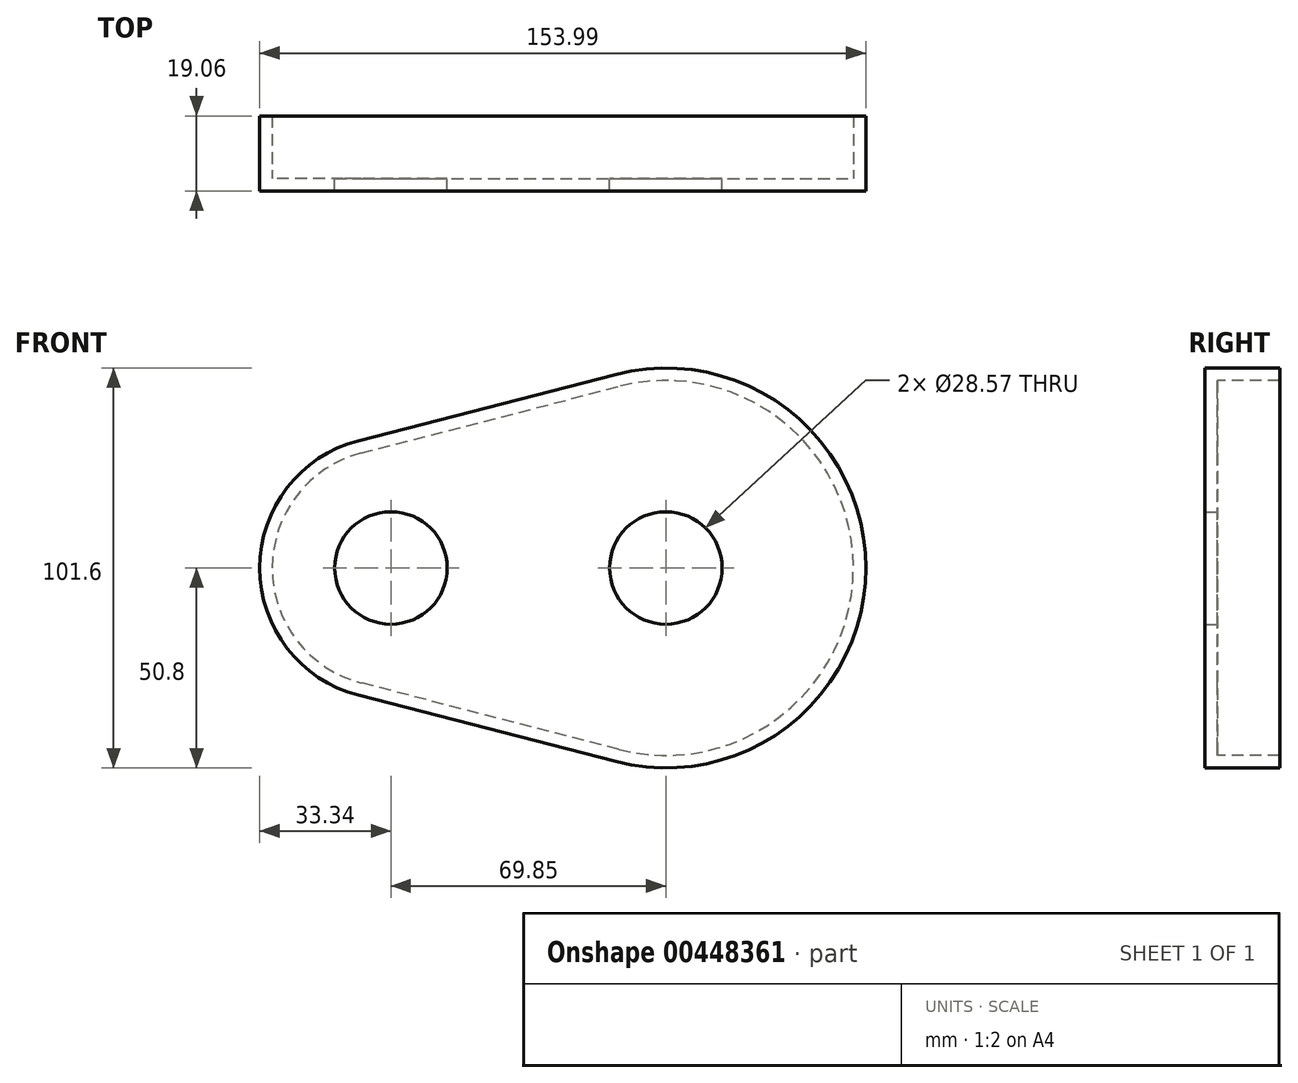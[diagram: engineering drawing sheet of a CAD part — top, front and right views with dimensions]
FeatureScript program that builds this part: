
annotation { "Feature Type Name" : "Feature", "Feature Type Description" : "" }
export const myFeature = defineFeature(function(context is Context, id is Id, definition is map)
    precondition{}
    {
        {
            var Q0;
            Q0=qCreatedBy(makeId("Front.planeOp"),FACE);
            var sketch = newSketch(context, id + "F0", { "sketchPlane" : qUnion([Q0])});
            skCircle(sketch, "E0", {"center": v(0, 0) * mm, "radius": 14.29 * mm});
            skLineSegment(sketch, "E1", {"start": v(0, 0) * mm, "end": v(-69.85, 0) * mm});
            skArc(sketch, "E2", {"start": v(-12.7, -49.19) * mm, "mid": v(50.8, 0) * mm, "end": v(-12.7, 49.19) * mm});
            skCircle(sketch, "E3", {"center": v(-69.85, 0) * mm, "radius": 14.29 * mm});
            skArc(sketch, "E4", {"start": v(-78.18, 32.28) * mm, "mid": v(-103.19, 0) * mm, "end": v(-78.18, -32.28) * mm});
            skLineSegment(sketch, "E5", {"start": v(-78.18, -32.28) * mm, "end": v(-12.7, -49.19) * mm});
            skLineSegment(sketch, "E6", {"start": v(-12.7, 49.19) * mm, "end": v(-78.18, 32.28) * mm});
            skSolve(sketch);
        }
        {
            var Q0;
            Q0=makeQuery(id+"F0.imprint","IMPRINT",FACE,{"disambiguationData":[TD([[makeQuery(id+"F0.imprint","IMPRINT",EDGE,{"derivedFrom":sQuery(id+"F0.wireOp",EDGE,"E0")}),-1.0]])]});
            extrude(context, id + "F1", {"entities" : qUnion([Q0]), "depth" : 3.17 * mm});
        }
        {
            var Q0;
            Q0=makeQuery(id+"F1.opExtrude","CAP_FACE",FACE,{"disambiguationData":[OSD([sQuery(id+"F0.wireOp",EDGE,"E0"),sQuery(id+"F0.wireOp",EDGE,"E2"),sQuery(id+"F0.wireOp",EDGE,"E3"),sQuery(id+"F0.wireOp",EDGE,"E4"),sQuery(id+"F0.wireOp",EDGE,"E5"),sQuery(id+"F0.wireOp",EDGE,"E6")])],"isStart":true});
            var sketch = newSketch(context, id + "F2", { "sketchPlane" : qUnion([Q0])});
            skLineSegment(sketch, "E7.0", {"start": v(77.4, 29.2) * mm, "end": v(11.9, 46.11) * mm});
            skArc(sketch, "E7.1", {"start": v(77.4, -29.2) * mm, "mid": v(100.01, 0) * mm, "end": v(77.4, 29.2) * mm});
            skLineSegment(sketch, "E7.2", {"start": v(11.9, -46.11) * mm, "end": v(77.4, -29.2) * mm});
            skArc(sketch, "E7.3", {"start": v(11.9, 46.11) * mm, "mid": v(-47.62, 0) * mm, "end": v(11.9, -46.11) * mm});
            skSolve(sketch);
        }
        {
            var Q0;
            Q0=makeQuery(id+"F2.imprint","IMPRINT",FACE,{"disambiguationData":[TD([[makeQuery(id+"F2.imprint","IMPRINT",EDGE,{"derivedFrom":sQuery(id+"F2.wireOp",EDGE,"E7.0")}),-1.0]])]});
            extrude(context, id + "F3", {"entities" : qUnion([Q0]), "operationType" : NewBodyOperationType.ADD, "depth" : 15.88 * mm});
        }
    });
